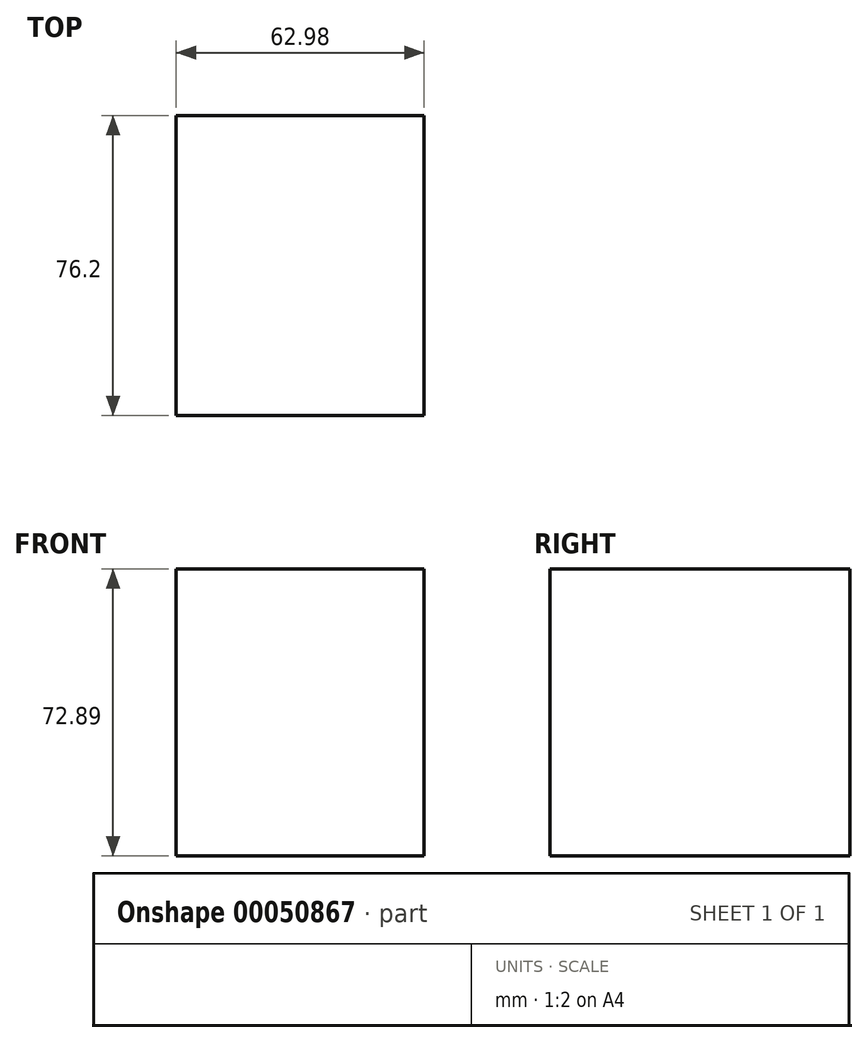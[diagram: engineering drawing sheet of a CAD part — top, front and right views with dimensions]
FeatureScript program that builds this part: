
annotation { "Feature Type Name" : "Feature", "Feature Type Description" : "" }
export const myFeature = defineFeature(function(context is Context, id is Id, definition is map)
    precondition{}
    {
        {
            var Q0;
            Q0=qCreatedBy(makeId("Front.planeOp"),FACE);
            var sketch = newSketch(context, id + "F0", { "sketchPlane" : qUnion([Q0])});
            skLineSegment(sketch, "E0.bottom", {"start": v(-90.8, 72.89) * mm, "end": v(-153.77, 72.89) * mm});
            skLineSegment(sketch, "E0.top", {"start": v(-90.8, 0) * mm, "end": v(-153.77, 0) * mm});
            skLineSegment(sketch, "E0.left", {"start": v(-90.8, 72.89) * mm, "end": v(-90.8, 0) * mm});
            skLineSegment(sketch, "E0.right", {"start": v(-153.77, 72.89) * mm, "end": v(-153.77, 0) * mm});
            skSolve(sketch);
        }
        {
            var Q0;
            Q0=makeQuery(id+"F0.imprint","IMPRINT",FACE,{"disambiguationData":[TD([[makeQuery(id+"F0.imprint","IMPRINT",EDGE,{"derivedFrom":sQuery(id+"F0.wireOp",EDGE,"E0.bottom")}),1.0]])]});
            extrude(context, id + "F1", {"entities" : qUnion([Q0]), "depth" : 76.2 * mm});
        }
        {
            var Q0;
            Q0=makeQuery(id+"F1.opExtrude","CAP_FACE",FACE,{"disambiguationData":[OSD([sQuery(id+"F0.wireOp",EDGE,"E0.bottom"),sQuery(id+"F0.wireOp",EDGE,"E0.top"),sQuery(id+"F0.wireOp",EDGE,"E0.left"),sQuery(id+"F0.wireOp",EDGE,"E0.right")])],"isStart":false});
            var sketch = newSketch(context, id + "F2", { "sketchPlane" : qUnion([Q0])});
            skCircle(sketch, "E1", {"center": v(-141.6, 58.18) * mm, "radius": 7.57 * mm});
            skCircle(sketch, "E2", {"center": v(-107.97, 58.53) * mm, "radius": 7.95 * mm});
            skCircle(sketch, "E3", {"center": v(-140.89, 25.79) * mm, "radius": 7.98 * mm});
            skCircle(sketch, "E4", {"center": v(-107.62, 25.79) * mm, "radius": 8.77 * mm});
            skSolve(sketch);
        }
        {
            var Q0;
            Q0=sQuery(id+"F2.wireOp",EDGE,"E1");
            var Q1;
            Q1=sQuery(id+"F2.wireOp",EDGE,"E3");
            var Q2;
            Q2=sQuery(id+"F2.wireOp",EDGE,"E4");
            var Q3;
            Q3=sQuery(id+"F2.wireOp",EDGE,"E2");
            extrude(context, id + "F3", {"bodyType" : ToolBodyType.SURFACE, "surfaceEntities" : qUnion([Q0, Q1, Q2, Q3]), "depth" : 25.4 * mm});
        }
    });
